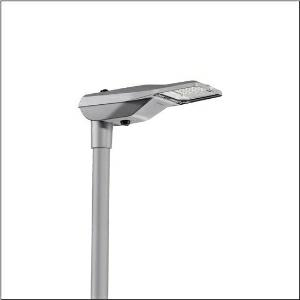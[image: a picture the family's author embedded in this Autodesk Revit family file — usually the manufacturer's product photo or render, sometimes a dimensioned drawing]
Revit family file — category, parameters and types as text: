
# Revit family: streetlight_sl_21_iq_micro___p0_8ab_5xe1r31y08db_c2fe
name_source: partatom
category: Lighting Fixtures
units: mm (PartAtom-declared; Revit-internal decimal feet)

## family parameters
Cut with Voids When Loaded = No
Host = Face
Light Source = No
Part Type = Normal
Room Calculation Point = No
Round Connector Dimension = Use Diameter
Shared = No

## types (1)
- --- (1 x LED, 4550 lm, 39.1 W, 3000K)
    Apparent Load = 39 VA
    CIE Flux Codes = 36 71 98 100 100
    Color Rendering = 70
    Color Temperature = 3000K
    Default Elevation = 1800 mm
    Description = Streetlight SL 21 iQ micro, mast luminaire, primary light control with lens, of PMMA, primary optical cover: cover, of toughened safety glass, transparent, light distribution: P0.8aB, light emission: direct distribution, primary light characteristic: asymmetric, installation type: post-top, side-entry, LED, High Power LED, rated luminous flux: 4.550lm, luminous efficacy: 116lm/W, light colour: 730, colour temperature: 3000K, control gear: iQ-Street Remote, D4i with power reduction, control: pre-setting: logarithmic dimming characteristic, Street-Remote, Auto-Match, Temp-Guard, Lumen-Switch, Night-Set, Smart-Wire, Light-Fading, Desk-Remote (wireless, voltage-free reading and setting of iQ features in the workshop via application-optimized NFC function/RFID function), optimised constant luminous flux control (CLO 2.0), mains connection: 220..240V, AC, 50/60Hz, start of lifetime: 39W, end of service life: 41W, reduction: 17W, luminaire housing, of diecast aluminium, powder-coated, Siteco® metallic grey (DB 702S), corrosivity category C5 mid according to DIN EN ISO 12944, please order mast flange separately, inclination adjustable: 0°, 5°, 10°, 15°, sealing non-destructively replaceable, multi-level sealing system, length: 528mm, width: 235mm, height: 110mm, mast flange for spigot size: 42mm (side-entry): 5XC10008XM4, 60/48mm (side-entry/post-top): 5XC10108XM2, 76/60mm (side-entry/post-top): 5XC10108XM1, mounting height: 4..8m, Smart Interface below and above, protection rating (complete): IP66, insulation class (complete): insulation class II (safety insulation), certification: CE, ENEC, ENEC+, VDE, impact resistance: IK10, permissible operating ambient temperature for outdoor applications: -40..+50°C, standard-compliant lighting for roads and squares, packaging unit: 1 piece

Light Distribution: P0.8aB
    Height = 110 mm
    Lamp = 1 x LED
    Lamp Light Flux = 4550 lm
    Lamp Power = 39.1 W
    Lamp count = 1
    Length = 528 mm
    Luminous efficacy = 116 lm/W
    Manufacturer = Siteco
    ModVariant = No
    Model = 5XE1R31Y08DB
    Number of Poles = 1
    OnlyDefault = Yes
    Power Factor = 1
    Product Name = Streetlight SL 21 iQ micro | P0.8aB
    Product group = mast luminaire | pylon top
    ProductGroupID = 6100
    Protection Class = Protection class II
    Protection Degree = IP 66
    RLX_Detail_Level = 1
    RLX_Emergency_Light_Flux = 0 lm
    RLX_Emergency_Type = 0
    RLX_Emergency_Type_DB = No
    RlxData = <blob elided: 97909 chars, md5=def006bd>
    Socket = socket
    Standby Power = 0 W
    System Light Flux = 4550 lm
    System Power = 39 W
    Type Comments = factory setting: luminous flux: 100 % | dim-lin: 254 | 765 mA
    Type Image = l_1007239.jpg
    URL = http://relux.com
    VarID = @adj_075544
    Voltage = 0 V
    Weight = 0.00 kg
    Width = 235 mm

## geometry (parser evidence)
native form markers: Blend x4, Sweep x11
no freeform markers — native parametric forms only
